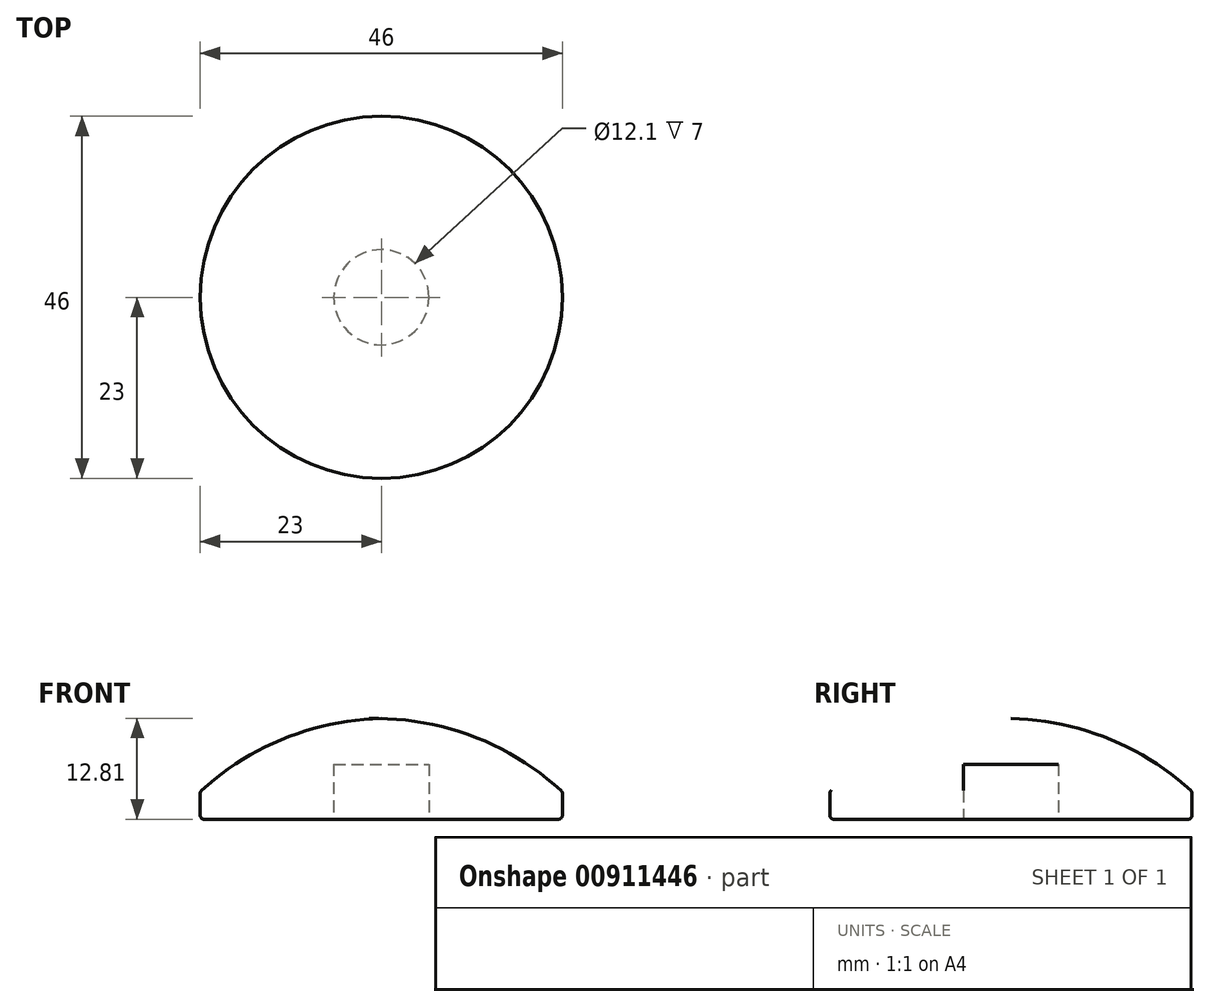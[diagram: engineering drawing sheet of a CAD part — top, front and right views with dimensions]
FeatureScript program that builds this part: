
annotation { "Feature Type Name" : "Feature", "Feature Type Description" : "" }
export const myFeature = defineFeature(function(context is Context, id is Id, definition is map)
    precondition{}
    {
        {
            var Q0;
            Q0=qCreatedBy(makeId("Front.planeOp"),FACE);
            var sketch = newSketch(context, id + "F0", { "sketchPlane" : qUnion([Q0])});
            skLineSegment(sketch, "E0", {"start": v(-23, 0) * mm, "end": v(-23, 3.5) * mm});
            skArc(sketch, "E1", {"start": v(0, 12.8) * mm, "mid": v(-12.35, 10.26) * mm, "end": v(-23, 3.5) * mm});
            skLineSegment(sketch, "E2", {"start": v(-23, 0) * mm, "end": v(0, 0) * mm});
            skLineSegment(sketch, "E3", {"start": v(0, 0) * mm, "end": v(0, 29.92) * mm, "construction": true});
            skLineSegment(sketch, "E4", {"start": v(0, 0) * mm, "end": v(0, 12.8) * mm});
            skSolve(sketch);
        }
        {
            var Q0;
            Q0 = qSketchRegion(id + "F0", true);
            var Q1;
            Q1=sQuery(id+"F0.wireOp",EDGE,"E3");
            revolve(context, id + "F1", {"surfaceOperationType" : NewSurfaceOperationType.NEW, "entities" : qUnion([Q0]), "axis" : qUnion([Q1]), "revolveType" : RevolveType.FULL});
        }
        {
            var Q0;
            Q0=makeQuery(id+"F1.opRevolve","SWEPT_FACE",FACE,{"disambiguationData":[OSD([sQuery(id+"F0.wireOp",EDGE,"E2")])]});
            var sketch = newSketch(context, id + "F2", { "sketchPlane" : qUnion([Q0])});
            skCircle(sketch, "E5", {"center": v(0, 0) * mm, "radius": 6.05 * mm});
            skSolve(sketch);
        }
        {
            var Q0;
            Q0 = qSketchRegion(id + "F2", true);
            extrude(context, id + "F3", {"entities" : qUnion([Q0]), "operationType" : NewBodyOperationType.REMOVE, "oppositeDirection" : true, "depth" : 7 * mm, "offsetDistance" : 25 * mm});
        }
        {
            var Q0;
            Q0=makeQuery(id+"F1.opRevolve","SWEPT_EDGE",EDGE,{"disambiguationData":[OSD([sQuery(id+"F0.wireOp",EDGE,"E0"),sQuery(id+"F0.wireOp",EDGE,"E2")])]});
            var Q1;
            Q1=makeQuery(id+"F1.opRevolve","SWEPT_EDGE",EDGE,{"disambiguationData":[OSD([sQuery(id+"F0.wireOp",EDGE,"E0"),sQuery(id+"F0.wireOp",EDGE,"E1")])]});
            fillet(context, id + "F4", {"entities" : qUnion([Q0, Q1]), "radius" : 0.5 * mm, "tangentPropagation" : true, "allowEdgeOverflow" : false});
        }
    });
